# Revit family: КСБ К2_ЕС_Eng
name_source: partatom
category: Mechanical Equipment
units: mm (PartAtom-declared; Revit-internal decimal feet)

## family parameters
Always vertical = Yes
Classification = None
Cut with Voids When Loaded = No
Part Type = Normal
Room Calculation Point = No
Round Connector Dimension = Use Diameter
Shared = No
Work Plane-Based = No

## types (24) — shared parameters
00_20_Manufacturer = Vents
00_20_Name = Sound-insulated fan
Casing Material = Steel, galvanized
Frequency = 50 Hz
Load Classification = HVAC
Maintenance zone material = <By Category>
Manufacturer = Vents
URL = https://ventilation-system.com
zero-valued in all types: Default Elevation

## per-type parameters (varying)
- KSB 100 К2: 00_20_Type=KSB 100 К2; A=414 mm; A11=80 mm  [stored 0.262467 ft]; A12=80 mm  [stored 0.262467 ft]; A2=507 mm; A21=47 mm  [stored 0.154199 ft]; Amperage=0 A; Apparent Load=58 VA; B=420 mm; B1=228 mm; BN=140 mm  [stored 0.459318 ft]; Diameter=100 mm  [stored 0.328084 ft]; Dn=105 mm  [stored 0.344488 ft]; Dy=100 mm  [stored 0.328084 ft]; H=258 mm; H11=139 mm  [stored 0.456037 ft]; H12=119 mm  [stored 0.39042 ft]; HN=75 mm; Height=258 mm; L=517 mm; Length=517 mm; Maximum Air Flow=285.0 m³/h; Number of Fase=1; Power=58 W; Sound pressure level at 3 m distance=34 dBA; Voltage=230 V; Weight=13.00 kg; Width=507 mm; b1=114 mm  [stored 0.374016 ft]
- KSB 500 К2 (∆): 00_20_Type=KSB  500 К2 (∆); A=1182 mm; A11=280 mm; A12=280 mm; A2=1263 mm; A21=41 mm  [stored 0.134514 ft]; Amperage=3 A; Apparent Load=649 VA; B=1203 mm; B1=993 mm; BN=401 mm; Diameter=500 mm; Dn=505 mm; Dy=500 mm; H=744 mm; H11=422 mm; H12=322 mm; HN=196 mm; Height=744 mm; L=1300 mm; Length=1300 mm; Maximum Air Flow=7000.0 m³/h; Number of Fase=1; Power=730 W; Sound pressure level at 3 m distance=56 dBA; Voltage=230 V; Weight=129.00 kg; Width=1263 mm; b1=497 mm
- KSB 125 К2: 00_20_Type=KSB 125 К2; A=414 mm; A11=93 mm; A12=93 mm; A2=507 mm; A21=47 mm  [stored 0.154199 ft]; Amperage=0 A; Apparent Load=64 VA; B=420 mm; B1=228 mm; BN=140 mm  [stored 0.459318 ft]; Diameter=125 mm  [stored 0.410105 ft]; Dn=130 mm  [stored 0.426509 ft]; Dy=125 mm  [stored 0.410105 ft]; H=258 mm; H11=142 mm; H12=117 mm; HN=75 mm; Height=258 mm; L=517 mm; Length=517 mm; Maximum Air Flow=330.0 m³/h; Number of Fase=1; Power=61 W; Sound pressure level at 3 m distance=35 dBA; Voltage=230 V; Weight=13.00 kg; Width=507 mm; b1=114 mm  [stored 0.374016 ft]
- KSB 125 К2 S: 00_20_Type=KSB 125 К2 S; A=525 mm; A11=93 mm; A12=93 mm; A2=617 mm; A21=46 mm  [stored 0.150919 ft]; Amperage=0 A; Apparent Load=85 VA; B=533 mm; B1=333 mm; BN=178 mm; Diameter=125 mm  [stored 0.410105 ft]; Dn=130 mm  [stored 0.426509 ft]; Dy=125 mm  [stored 0.410105 ft]; H=280 mm; H11=153 mm; H12=128 mm; HN=80 mm  [stored 0.262467 ft]; Height=280 mm; L=630 mm; Length=630 mm; Maximum Air Flow=848.0 m³/h; Number of Fase=1; Power=88 W; Sound pressure level at 3 m distance=40 dBA; Voltage=230 V; Weight=19.00 kg; Width=617 mm; b1=167 mm
- KSB 150 К2: 00_20_Type=KSB 150 К2; A=493 mm; A11=105 mm  [stored 0.344488 ft]; A12=105 mm  [stored 0.344488 ft]; A2=586 mm; A21=47 mm  [stored 0.154199 ft]; Amperage=0 A; Apparent Load=85 VA; B=470 mm; B1=278 mm; BN=157 mm  [stored 0.515092 ft]; Diameter=150 mm; Dn=155 mm  [stored 0.50853 ft]; Dy=150 mm; H=282 mm; H11=156 mm  [stored 0.511811 ft]; H12=126 mm  [stored 0.413386 ft]; HN=81 mm; Height=282 mm; L=566 mm; Length=566 mm; Maximum Air Flow=485.0 m³/h; Number of Fase=1; Power=84 W; Sound pressure level at 3 m distance=38 dBA; Voltage=230 V; Weight=17.00 kg; Width=586 mm; b1=139 mm  [stored 0.456037 ft]
- KSB 160 К2: 00_20_Type=KSB 160 К2; A=493 mm; A11=110 mm  [stored 0.360892 ft]; A12=110 mm  [stored 0.360892 ft]; A2=586 mm; A21=47 mm  [stored 0.154199 ft]; Amperage=0 A; Apparent Load=87 VA; B=470 mm; B1=278 mm; BN=157 mm  [stored 0.515092 ft]; Diameter=160 mm  [stored 0.524934 ft]; Dn=165 mm; Dy=160 mm  [stored 0.524934 ft]; H=282 mm; H11=157 mm  [stored 0.515092 ft]; H12=125 mm  [stored 0.410105 ft]; HN=81 mm; Height=282 mm; L=566 mm; Length=566 mm; Maximum Air Flow=500.0 m³/h; Number of Fase=1; Power=86 W; Sound pressure level at 3 m distance=38 dBA; Voltage=230 V; Weight=17.00 kg; Width=586 mm; b1=139 mm  [stored 0.456037 ft]
- KSB 200 К2: 00_20_Type=KSB 200 К2; A=535 mm; A11=130 mm  [stored 0.426509 ft]; A12=130 mm  [stored 0.426509 ft]; A2=628 mm; A21=47 mm  [stored 0.154199 ft]; Amperage=1 A; Apparent Load=163 VA; B=535 mm; B1=358 mm; BN=178 mm; Diameter=200 mm; Dn=205 mm; Dy=200 mm; H=355 mm; H11=198 mm; H12=158 mm; HN=99 mm; Height=355 mm; L=632 mm; Length=632 mm; Maximum Air Flow=770.0 m³/h; Number of Fase=1; Power=164 W; Sound pressure level at 3 m distance=42 dBA; Voltage=230 V; Weight=22.60 kg; Width=628 mm; b1=179 mm
- KSB 250 К2: 00_20_Type=KSB 250 К2; A=666 mm; A11=155 mm  [stored 0.50853 ft]; A12=155 mm  [stored 0.50853 ft]; A2=759 mm; A21=47 mm  [stored 0.154199 ft]; Amperage=1 A; Apparent Load=322 VA; B=677 mm; B1=537 mm; BN=226 mm; Diameter=250 mm; Dn=255 mm; Dy=250 mm; H=429 mm; H11=240 mm; H12=190 mm; HN=117 mm; Height=429 mm; L=774 mm; Length=774 mm; Maximum Air Flow=1515.0 m³/h; Number of Fase=1; Power=320 W; Sound pressure level at 3 m distance=45 dBA; Voltage=230 V; Weight=33.00 kg; Width=759 mm; b1=269 mm
- KSB 315 К2 S: 00_20_Type=KSB 315 К2 S; A=666 mm; A11=188 mm; A12=188 mm; A2=747 mm; A21=41 mm  [stored 0.134514 ft]; Amperage=1 A; Apparent Load=440 VA; B=760 mm; B1=560 mm; BN=253 mm; Diameter=315 mm; Dn=320 mm; Dy=315 mm; H=460 mm; H11=262 mm; H12=199 mm; HN=125 mm  [stored 0.410105 ft]; Height=460 mm; L=857 mm; Length=857 mm; Maximum Air Flow=2710.0 m³/h; Number of Fase=3; Power=645 W; Sound pressure level at 3 m distance=48 dBA; Voltage=400 V; Weight=48.00 kg; Width=747 mm; b1=280 mm
- KSB 355 К2: 00_20_Type=KSB 355 К2; A=804 mm; A11=208 mm; A12=208 mm; A2=885 mm; A21=41 mm  [stored 0.134514 ft]; Amperage=1 A; Apparent Load=205 VA; B=830 mm; B1=641 mm; BN=277 mm; Diameter=355 mm; Dn=360 mm; Dy=355 mm; H=500 mm; H11=286 mm; H12=215 mm; HN=135 mm  [stored 0.442913 ft]; Height=500 mm; L=927 mm; Length=927 mm; Maximum Air Flow=2235.0 m³/h; Number of Fase=1; Power=202 W; Sound pressure level at 3 m distance=48 dBA; Voltage=230 V; Weight=58.00 kg; Width=885 mm; b1=321 mm
- KSB 400 К2: 00_20_Type=KSB 400 К2; A=876 mm; A11=230 mm; A12=230 mm; A2=957 mm; A21=41 mm  [stored 0.134514 ft]; Amperage=2 A; Apparent Load=460 VA; B=927 mm; B1=737 mm; BN=309 mm; Diameter=400 mm; Dn=405 mm; Dy=400 mm; H=578 mm; H11=329 mm; H12=249 mm; HN=155 mm  [stored 0.50853 ft]; Height=578 mm; L=1024 mm; Length=1024 mm; Maximum Air Flow=2860.0 m³/h; Number of Fase=1; Power=349 W; Sound pressure level at 3 m distance=48 dBA; Voltage=230 V; Weight=78.50 kg; Width=957 mm; b1=369 mm
- KSB 450 К2 Б: 00_20_Type=KSB 450 К2 Б; A=968 mm; A11=255 mm; A12=255 mm; A2=1049 mm; A21=41 mm  [stored 0.134514 ft]; Amperage=2 A; Apparent Load=541 VA; B=1049 mm; B1=858 mm; BN=350 mm; Diameter=450 mm; Dn=455 mm; Dy=450 mm; H=607 mm; H11=349 mm; H12=259 mm; HN=162 mm; Height=607 mm; L=1152 mm; Length=1152 mm; Maximum Air Flow=2760.0 m³/h; Number of Fase=1; Power=473 W; Sound pressure level at 3 m distance=48 dBA; Voltage=230 V; Weight=84.00 kg; Width=1049 mm; b1=429 mm
- KSB 500 К2 (Y): 00_20_Type=KSB 500 К2 (Y); A=1182 mm; A11=280 mm; A12=280 mm; A2=1263 mm; A21=41 mm  [stored 0.134514 ft]; Amperage=2 A; Apparent Load=640 VA; B=1203 mm; B1=993 mm; BN=401 mm; Diameter=500 mm; Dn=505 mm; Dy=500 mm; H=744 mm; H11=422 mm; H12=322 mm; HN=196 mm; Height=744 mm; L=1300 mm; Length=1300 mm; Maximum Air Flow=6720.0 m³/h; Number of Fase=3; Power=780 W; Sound pressure level at 3 m distance=54 dBA; Voltage=400 V; Weight=129.00 kg; Width=1263 mm; b1=497 mm
- KSB 100 К2 ЕС: 00_20_Type=KSB 100 К2 ЕС; A=414 mm; A11=80 mm  [stored 0.262467 ft]; A12=80 mm  [stored 0.262467 ft]; A2=507 mm; A21=47 mm  [stored 0.154199 ft]; Amperage=1 A; Apparent Load=127 VA; B=420 mm; B1=228 mm; BN=140 mm  [stored 0.459318 ft]; Diameter=100 mm  [stored 0.328084 ft]; Dn=105 mm  [stored 0.344488 ft]; Dy=100 mm  [stored 0.328084 ft]; H=270 mm; H11=145 mm  [stored 0.475722 ft]; H12=125 mm  [stored 0.410105 ft]; HN=78 mm; Height=270 mm; L=517 mm; Length=517 mm; Maximum Air Flow=341.0 m³/h; Number of Fase=1; Power=69 W; Sound pressure level at 3 m distance=37 dBA; Voltage=230 V; Weight=12.00 kg; Width=507 mm; b1=114 mm  [stored 0.374016 ft]
- KSB 125 К2 ЕС: 00_20_Type=KSB 125 К2 ЕС; A=414 mm; A11=93 mm; A12=93 mm; A2=507 mm; A21=47 mm  [stored 0.154199 ft]; Amperage=1 A; Apparent Load=133 VA; B=420 mm; B1=228 mm; BN=140 mm  [stored 0.459318 ft]; Diameter=125 mm  [stored 0.410105 ft]; Dn=130 mm  [stored 0.426509 ft]; Dy=125 mm  [stored 0.410105 ft]; H=270 mm; H11=148 mm; H12=123 mm; HN=78 mm; Height=270 mm; L=517 mm; Length=517 mm; Maximum Air Flow=444.0 m³/h; Number of Fase=1; Power=78 W; Sound pressure level at 3 m distance=39 dBA; Voltage=230 V; Weight=12.00 kg; Width=507 mm; b1=114 mm  [stored 0.374016 ft]
- KSB 150 К2 ЕС: 00_20_Type=KSB 150 К2 ЕС; A=414 mm; A11=105 mm  [stored 0.344488 ft]; A12=105 mm  [stored 0.344488 ft]; A2=507 mm; A21=47 mm  [stored 0.154199 ft]; Amperage=1 A; Apparent Load=136 VA; B=420 mm; B1=228 mm; BN=140 mm  [stored 0.459318 ft]; Diameter=150 mm; Dn=155 mm  [stored 0.50853 ft]; Dy=150 mm; H=270 mm; H11=150 mm; H12=120 mm  [stored 0.393701 ft]; HN=78 mm; Height=270 mm; L=517 mm; Length=517 mm; Maximum Air Flow=495.0 m³/h; Number of Fase=1; Power=81 W; Sound pressure level at 3 m distance=40 dBA; Voltage=230 V; Weight=12.00 kg; Width=507 mm; b1=114 mm  [stored 0.374016 ft]
- KSB 160 К2 ЕС: 00_20_Type=KSB 160 К2 ЕС; A=414 mm; A11=110 mm  [stored 0.360892 ft]; A12=110 mm  [stored 0.360892 ft]; A2=507 mm; A21=47 mm  [stored 0.154199 ft]; Amperage=1 A; Apparent Load=138 VA; B=420 mm; B1=228 mm; BN=140 mm  [stored 0.459318 ft]; Diameter=160 mm  [stored 0.524934 ft]; Dn=165 mm; Dy=160 mm  [stored 0.524934 ft]; H=270 mm; H11=151 mm  [stored 0.495407 ft]; H12=119 mm  [stored 0.39042 ft]; HN=78 mm; Height=270 mm; L=517 mm; Length=517 mm; Maximum Air Flow=454.0 m³/h; Number of Fase=1; Power=85 W; Sound pressure level at 3 m distance=40 dBA; Voltage=230 V; Weight=12.00 kg; Width=507 mm; b1=114 mm  [stored 0.374016 ft]
- KSB 200 К2 ЕС: 00_20_Type=KSB 200 К2 ЕС; A=553 mm; A11=130 mm  [stored 0.426509 ft]; A12=130 mm  [stored 0.426509 ft]; A2=646 mm; A21=46 mm  [stored 0.150919 ft]; Amperage=1 A; Apparent Load=202 VA; B=551 mm; B1=374 mm; BN=184 mm; Diameter=200 mm; Dn=205 mm; Dy=200 mm; H=328 mm; H11=184 mm; H12=144 mm  [stored 0.472441 ft]; HN=92 mm  [stored 0.301837 ft]; Height=328 mm; L=648 mm; Length=648 mm; Maximum Air Flow=740.0 m³/h; Number of Fase=1; Power=111 W; Sound pressure level at 3 m distance=42 dBA; Voltage=230 V; Weight=20.00 kg; Width=646 mm; b1=187 mm
- KSB 250 К2 ЕС: 00_20_Type=KSB 250 К2 ЕС; A=616 mm; A11=155 mm  [stored 0.50853 ft]; A12=155 mm  [stored 0.50853 ft]; A2=709 mm; A21=47 mm  [stored 0.154199 ft]; Amperage=1 A; Apparent Load=304 VA; B=665 mm; B1=487 mm; BN=222 mm; Diameter=250 mm; Dn=255 mm; Dy=250 mm; H=371 mm; H11=211 mm; H12=161 mm; HN=103 mm; Height=371 mm; L=762 mm; Length=762 mm; Maximum Air Flow=1099.0 m³/h; Number of Fase=1; Power=164 W; Sound pressure level at 3 m distance=45 dBA; Voltage=230 V; Weight=27.00 kg; Width=709 mm; b1=244 mm
- KSB 315 К2 ЕС: 00_20_Type=KSB 315 К2 ЕС; A=737 mm; A11=188 mm; A12=188 mm; A2=818 mm; A21=41 mm  [stored 0.134514 ft]; Amperage=2 A; Apparent Load=534 VA; B=807 mm; B1=600 mm; BN=269 mm; Diameter=315 mm; Dn=320 mm; Dy=315 mm; H=505 mm; H11=284 mm; H12=221 mm; HN=136 mm; Height=505 mm; L=904 mm; Length=904 mm; Maximum Air Flow=3053.0 m³/h; Number of Fase=1; Power=531 W; Sound pressure level at 3 m distance=47 dBA; Voltage=230 V; Weight=47.00 kg; Width=818 mm; b1=300 mm
- KSB 355 К2 ЕС: 00_20_Type=KSB 355 К2 ЕС; A=737 mm; A11=208 mm; A12=208 mm; A2=818 mm; A21=41 mm  [stored 0.134514 ft]; Amperage=2 A; Apparent Load=531 VA; B=807 mm; B1=600 mm; BN=269 mm; Diameter=355 mm; Dn=360 mm; Dy=355 mm; H=505 mm; H11=288 mm; H12=217 mm; HN=136 mm; Height=505 mm; L=904 mm; Length=904 mm; Maximum Air Flow=3417.0 m³/h; Number of Fase=1; Power=527 W; Sound pressure level at 3 m distance=48 dBA; Voltage=230 V; Weight=50.00 kg; Width=818 mm; b1=300 mm
- KSB 400 К2 ЕС: 00_20_Type=KSB 400 К2 ЕС; A=737 mm; A11=230 mm; A12=230 mm; A2=818 mm; A21=41 mm  [stored 0.134514 ft]; Amperage=2 A; Apparent Load=518 VA; B=807 mm; B1=600 mm; BN=269 mm; Diameter=400 mm; Dn=405 mm; Dy=400 mm; H=505 mm; H11=293 mm; H12=213 mm; HN=136 mm; Height=505 mm; L=904 mm; Length=904 mm; Maximum Air Flow=3633.0 m³/h; Number of Fase=1; Power=513 W; Sound pressure level at 3 m distance=48 dBA; Voltage=230 V; Weight=51.00 kg; Width=818 mm; b1=300 mm
- KSB 450 К2 ЕС: 00_20_Type=KSB 450 К2 ЕС; A=805 mm; A11=255 mm; A12=255 mm; A2=886 mm; A21=41 mm  [stored 0.134514 ft]; Amperage=2 A; Apparent Load=449 VA; B=885 mm; B1=670 mm; BN=295 mm; Diameter=450 mm; Dn=455 mm; Dy=450 mm; H=580 mm; H11=335 mm; H12=245 mm; HN=155 mm  [stored 0.50853 ft]; Height=580 mm; L=982 mm; Length=982 mm; Maximum Air Flow=5620.0 m³/h; Number of Fase=1; Power=1200 W; Sound pressure level at 3 m distance=54 dBA; Voltage=230 V; Weight=60.00 kg; Width=886 mm; b1=335 mm
- KSB 500 К2 ЕС: 00_20_Type=KSB 500 К2 ЕС; A=998 mm; A11=280 mm; A12=280 mm; A2=1079 mm; A21=41 mm  [stored 0.134514 ft]; Amperage=3 A; Apparent Load=787 VA; B=1049 mm; B1=800 mm; BN=350 mm; Diameter=500 mm; Dn=505 mm; Dy=500 mm; H=660 mm; H11=380 mm; H12=280 mm; HN=175 mm; Height=660 mm; L=1146 mm; Length=1146 mm; Maximum Air Flow=7145.0 m³/h; Number of Fase=1; Power=752 W; Sound pressure level at 3 m distance=56 dBA; Voltage=230 V; Weight=76.00 kg; Width=1079 mm; b1=400 mm

note: [stored X ft] marks values corroborated as IEEE doubles in the binary element streams (Revit-internal decimal feet)
